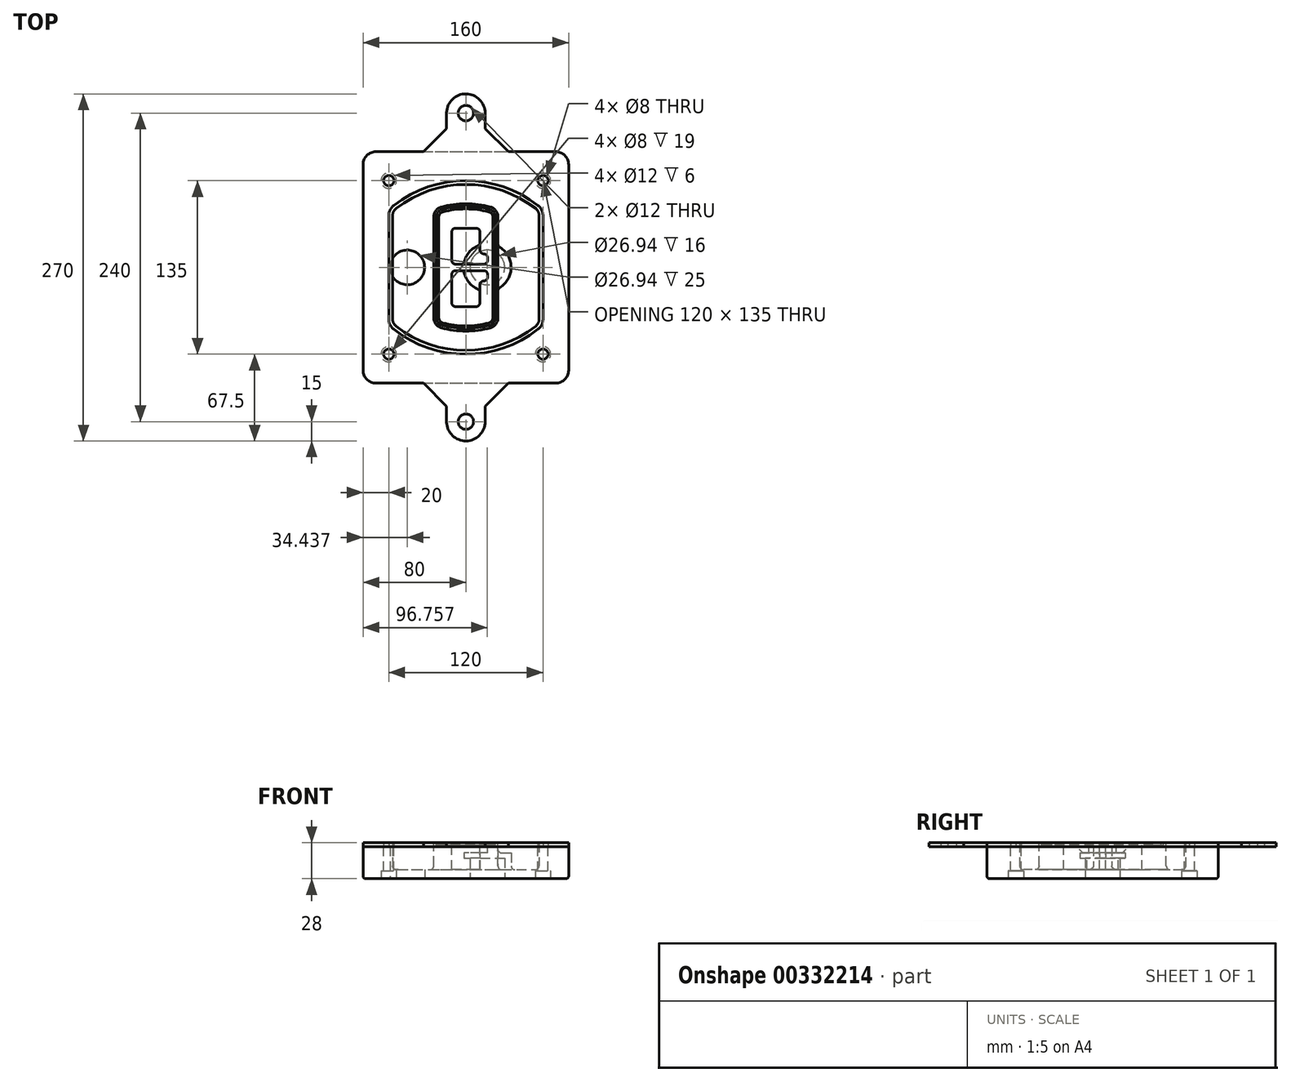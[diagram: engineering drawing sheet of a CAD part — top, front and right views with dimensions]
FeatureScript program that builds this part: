
annotation { "Feature Type Name" : "Feature", "Feature Type Description" : "" }
export const myFeature = defineFeature(function(context is Context, id is Id, definition is map)
    precondition{}
    {
        {
            var Q0;
            Q0=qCreatedBy(makeId("Top.planeOp"),FACE);
            var sketch = newSketch(context, id + "F0", { "sketchPlane" : qUnion([Q0])});
            skPoint(sketch, "E0.rect.middle", {"position": v(0, 0) * mm});
            skLineSegment(sketch, "E1.bottom", {"start": v(-70, -90) * mm, "end": v(70, -90) * mm});
            skLineSegment(sketch, "E1.top", {"start": v(-70, 90) * mm, "end": v(70, 90) * mm});
            skLineSegment(sketch, "E1.left", {"start": v(-80, -80) * mm, "end": v(-80, 80) * mm});
            skLineSegment(sketch, "E1.right", {"start": v(80, -80) * mm, "end": v(80, 80) * mm});
            skLineSegment(sketch, "E2", {"start": v(-80, 90) * mm, "end": v(80, -90) * mm, "construction": true});
            skLineSegment(sketch, "E3", {"start": v(80, 90) * mm, "end": v(-80, -90) * mm, "construction": true});
            skCircle(sketch, "E4", {"center": v(-60, 67.5) * mm, "radius": 4 * mm});
            skCircle(sketch, "E5", {"center": v(60, 67.5) * mm, "radius": 4 * mm});
            skCircle(sketch, "E6", {"center": v(60, -67.5) * mm, "radius": 4 * mm});
            skCircle(sketch, "E7", {"center": v(-60, -67.5) * mm, "radius": 4 * mm});
            skLineSegment(sketch, "E8", {"start": v(-60, 67.5) * mm, "end": v(60, 67.5) * mm, "construction": true});
            skLineSegment(sketch, "E9", {"start": v(60, 67.5) * mm, "end": v(60, -67.5) * mm, "construction": true});
            skLineSegment(sketch, "E10", {"start": v(60, -67.5) * mm, "end": v(-60, -67.5) * mm, "construction": true});
            skLineSegment(sketch, "E11", {"start": v(-60, -67.5) * mm, "end": v(-60, 67.5) * mm, "construction": true});
            skLineSegment(sketch, "E12", {"start": v(-60, 40.3) * mm, "end": v(-60, -40.3) * mm});
            skLineSegment(sketch, "E13", {"start": v(60, 40.3) * mm, "end": v(60, -40.3) * mm});
            skArc(sketch, "E14", {"start": v(56.15, 48.18) * mm, "mid": v(0, 67.5) * mm, "end": v(-56.15, 48.18) * mm});
            skArc(sketch, "E15", {"start": v(-56.15, -48.18) * mm, "mid": v(0, -67.5) * mm, "end": v(56.15, -48.18) * mm});
            skLineSegment(sketch, "E16", {"start": v(-60, 0) * mm, "end": v(60, 0) * mm, "construction": true});
            skPoint(sketch, "E17.visualSharp", {"position": v(-60, -45) * mm});
            skArc(sketch, "E17.filletArc", {"start": v(-60, -40.3) * mm, "mid": v(-58.99, -44.68) * mm, "end": v(-56.15, -48.18) * mm});
            skPoint(sketch, "E18.visualSharp", {"position": v(-60, 45) * mm});
            skArc(sketch, "E18.filletArc", {"start": v(-56.15, 48.18) * mm, "mid": v(-58.99, 44.68) * mm, "end": v(-60, 40.3) * mm});
            skPoint(sketch, "E19.visualSharp", {"position": v(60, 45) * mm});
            skArc(sketch, "E19.filletArc", {"start": v(60, 40.3) * mm, "mid": v(58.99, 44.68) * mm, "end": v(56.15, 48.18) * mm});
            skPoint(sketch, "E20.visualSharp", {"position": v(60, -45) * mm});
            skArc(sketch, "E20.filletArc", {"start": v(56.15, -48.18) * mm, "mid": v(58.99, -44.68) * mm, "end": v(60, -40.3) * mm});
            skPoint(sketch, "E21.visualSharp", {"position": v(-80, 90) * mm});
            skArc(sketch, "E21.filletArc", {"start": v(-70, 90) * mm, "mid": v(-77.07, 87.07) * mm, "end": v(-80, 80) * mm});
            skPoint(sketch, "E22.visualSharp", {"position": v(80, 90) * mm});
            skArc(sketch, "E22.filletArc", {"start": v(80, 80) * mm, "mid": v(77.07, 87.07) * mm, "end": v(70, 90) * mm});
            skPoint(sketch, "E23.visualSharp", {"position": v(80, -90) * mm});
            skArc(sketch, "E23.filletArc", {"start": v(70, -90) * mm, "mid": v(77.07, -87.07) * mm, "end": v(80, -80) * mm});
            skPoint(sketch, "E24.visualSharp", {"position": v(-80, -90) * mm});
            skArc(sketch, "E24.filletArc", {"start": v(-80, -80) * mm, "mid": v(-77.07, -87.07) * mm, "end": v(-70, -90) * mm});
            skArc(sketch, "E25.0", {"start": v(57, 40.3) * mm, "mid": v(56.3, 43.36) * mm, "end": v(54.3, 45.81) * mm});
            skLineSegment(sketch, "E25.1", {"start": v(57, 40.3) * mm, "end": v(57, -40.3) * mm});
            skArc(sketch, "E25.2", {"start": v(54.3, -45.81) * mm, "mid": v(56.3, -43.36) * mm, "end": v(57, -40.3) * mm});
            skArc(sketch, "E25.3", {"start": v(-54.3, -45.81) * mm, "mid": v(0, -64.5) * mm, "end": v(54.3, -45.81) * mm});
            skArc(sketch, "E25.4", {"start": v(-57, -40.3) * mm, "mid": v(-56.3, -43.36) * mm, "end": v(-54.3, -45.81) * mm});
            skArc(sketch, "E25.5", {"start": v(54.3, 45.81) * mm, "mid": v(0, 64.5) * mm, "end": v(-54.3, 45.81) * mm});
            skLineSegment(sketch, "E25.6", {"start": v(-57, 40.3) * mm, "end": v(-57, -40.3) * mm});
            skArc(sketch, "E25.7", {"start": v(-54.3, 45.81) * mm, "mid": v(-56.3, 43.36) * mm, "end": v(-57, 40.3) * mm});
            skArc(sketch, "E26.0", {"start": v(-58.62, 51.33) * mm, "mid": v(-62.58, 46.43) * mm, "end": v(-64, 40.3) * mm});
            skArc(sketch, "E26.1", {"start": v(58.62, 51.33) * mm, "mid": v(0, 71.5) * mm, "end": v(-58.62, 51.33) * mm});
            skArc(sketch, "E26.2", {"start": v(64, 40.3) * mm, "mid": v(62.58, 46.43) * mm, "end": v(58.62, 51.33) * mm});
            skLineSegment(sketch, "E26.3", {"start": v(64, 40.3) * mm, "end": v(64, -40.3) * mm});
            skArc(sketch, "E26.4", {"start": v(58.62, -51.33) * mm, "mid": v(62.58, -46.43) * mm, "end": v(64, -40.3) * mm});
            skLineSegment(sketch, "E26.5", {"start": v(-64, 40.3) * mm, "end": v(-64, -40.3) * mm});
            skArc(sketch, "E26.6", {"start": v(-58.62, -51.33) * mm, "mid": v(0, -71.5) * mm, "end": v(58.62, -51.33) * mm});
            skArc(sketch, "E26.7", {"start": v(-64, -40.3) * mm, "mid": v(-62.58, -46.43) * mm, "end": v(-58.62, -51.33) * mm});
            skSolve(sketch);
        }
        {
            var Q0;
            Q0=makeQuery(id+"F0.imprint","IMPRINT",FACE,{"disambiguationData":[TD([[makeQuery(id+"F0.imprint","IMPRINT",EDGE,{"derivedFrom":sQuery(id+"F0.wireOp",EDGE,"E1.bottom")}),1.0]])]});
            var Q1;
            Q1=makeQuery(id+"F0.imprint","IMPRINT",FACE,{"disambiguationData":[TD([[makeQuery(id+"F0.imprint","IMPRINT",EDGE,{"derivedFrom":sQuery(id+"F0.wireOp",EDGE,"E12")}),1.0]])]});
            var Q2;
            Q2=makeQuery(id+"F0.imprint","IMPRINT",FACE,{"disambiguationData":[TD([[makeQuery(id+"F0.imprint","IMPRINT",EDGE,{"derivedFrom":sQuery(id+"F0.wireOp",EDGE,"E25.0")}),1.0]])]});
            var Q3;
            Q3=makeQuery(id+"F0.imprint","IMPRINT",FACE,{"disambiguationData":[TD([[makeQuery(id+"F0.imprint","IMPRINT",EDGE,{"derivedFrom":sQuery(id+"F0.wireOp",EDGE,"E12")}),-1.0]])]});
            extrude(context, id + "F1", {"entities" : qUnion([Q0, Q1, Q2, Q3]), "oppositeDirection" : true, "depth" : 25 * mm});
        }
        {
            var Q0;
            Q0=makeQuery(id+"F0.imprint","IMPRINT",FACE,{"disambiguationData":[TD([[makeQuery(id+"F0.imprint","IMPRINT",EDGE,{"derivedFrom":sQuery(id+"F0.wireOp",EDGE,"E12")}),1.0]])]});
            extrude(context, id + "F2", {"entities" : qUnion([Q0]), "operationType" : NewBodyOperationType.ADD, "depth" : 3 * mm});
        }
        {
            var Q0;
            Q0=makeQuery(id+"F0.imprint","IMPRINT",FACE,{"disambiguationData":[TD([[makeQuery(id+"F0.imprint","IMPRINT",EDGE,{"derivedFrom":sQuery(id+"F0.wireOp",EDGE,"E25.0")}),1.0]])]});
            extrude(context, id + "F3", {"entities" : qUnion([Q0]), "operationType" : NewBodyOperationType.REMOVE, "oppositeDirection" : true, "depth" : 18 * mm});
        }
        {
            var Q0;
            Q0=makeQuery(id+"F2.opExtrude","CAP_FACE",FACE,{"disambiguationData":[OSD([sQuery(id+"F0.wireOp",EDGE,"E12"),sQuery(id+"F0.wireOp",EDGE,"E13"),sQuery(id+"F0.wireOp",EDGE,"E14"),sQuery(id+"F0.wireOp",EDGE,"E15"),sQuery(id+"F0.wireOp",EDGE,"E17.filletArc"),sQuery(id+"F0.wireOp",EDGE,"E18.filletArc"),sQuery(id+"F0.wireOp",EDGE,"E19.filletArc"),sQuery(id+"F0.wireOp",EDGE,"E20.filletArc"),sQuery(id+"F0.wireOp",EDGE,"E25.0"),sQuery(id+"F0.wireOp",EDGE,"E25.1"),sQuery(id+"F0.wireOp",EDGE,"E25.2"),sQuery(id+"F0.wireOp",EDGE,"E25.3"),sQuery(id+"F0.wireOp",EDGE,"E25.4"),sQuery(id+"F0.wireOp",EDGE,"E25.5"),sQuery(id+"F0.wireOp",EDGE,"E25.6"),sQuery(id+"F0.wireOp",EDGE,"E25.7")])],"isStart":false});
            var sketch = newSketch(context, id + "F4", { "sketchPlane" : qUnion([Q0])});
            skArc(sketch, "E27.0", {"start": v(-19.08, -46.97) * mm, "mid": v(0, -49.5) * mm, "end": v(19.08, -46.97) * mm});
            skArc(sketch, "E28.0", {"start": v(19.08, 46.97) * mm, "mid": v(0, 49.5) * mm, "end": v(-19.08, 46.97) * mm});
            skLineSegment(sketch, "E29", {"start": v(-25, 39.25) * mm, "end": v(-25, -39.25) * mm});
            skLineSegment(sketch, "E30", {"start": v(25, 39.25) * mm, "end": v(25, -39.25) * mm});
            skLineSegment(sketch, "E31", {"start": v(-25, 45.1) * mm, "end": v(25, 45.1) * mm, "construction": true});
            skLineSegment(sketch, "E32", {"start": v(-25, -45.1) * mm, "end": v(25, -45.1) * mm, "construction": true});
            skPoint(sketch, "E33.visualSharp", {"position": v(-25, 45.1) * mm});
            skArc(sketch, "E33.filletArc", {"start": v(-19.08, 46.97) * mm, "mid": v(-23.35, 44.11) * mm, "end": v(-25, 39.25) * mm});
            skPoint(sketch, "E34.visualSharp", {"position": v(25, 45.1) * mm});
            skArc(sketch, "E34.filletArc", {"start": v(25, 39.25) * mm, "mid": v(23.35, 44.11) * mm, "end": v(19.08, 46.97) * mm});
            skPoint(sketch, "E35.visualSharp", {"position": v(25, -45.1) * mm});
            skArc(sketch, "E35.filletArc", {"start": v(19.08, -46.97) * mm, "mid": v(23.35, -44.11) * mm, "end": v(25, -39.25) * mm});
            skPoint(sketch, "E36.visualSharp", {"position": v(-25, -45.1) * mm});
            skArc(sketch, "E36.filletArc", {"start": v(-25, -39.25) * mm, "mid": v(-23.35, -44.11) * mm, "end": v(-19.08, -46.97) * mm});
            skArc(sketch, "E37.0", {"start": v(54.3, 45.81) * mm, "mid": v(0, 64.5) * mm, "end": v(-54.3, 45.81) * mm});
            skArc(sketch, "E37.1", {"start": v(-54.3, 45.81) * mm, "mid": v(-56.3, 43.36) * mm, "end": v(-57, 40.3) * mm});
            skLineSegment(sketch, "E37.2", {"start": v(-57, 40.3) * mm, "end": v(-57, -40.3) * mm});
            skArc(sketch, "E37.3", {"start": v(-57, -40.3) * mm, "mid": v(-56.3, -43.36) * mm, "end": v(-54.3, -45.81) * mm});
            skArc(sketch, "E37.4", {"start": v(-54.3, -45.81) * mm, "mid": v(0, -64.5) * mm, "end": v(54.3, -45.81) * mm});
            skArc(sketch, "E37.5", {"start": v(54.3, -45.81) * mm, "mid": v(56.3, -43.36) * mm, "end": v(57, -40.3) * mm});
            skLineSegment(sketch, "E37.6", {"start": v(57, 40.3) * mm, "end": v(57, -40.3) * mm});
            skArc(sketch, "E37.7", {"start": v(57, 40.3) * mm, "mid": v(56.3, 43.36) * mm, "end": v(54.3, 45.81) * mm});
            skLineSegment(sketch, "E38.0", {"start": v(23, 39.25) * mm, "end": v(23, -39.25) * mm});
            skArc(sketch, "E38.1", {"start": v(18.56, -45.04) * mm, "mid": v(21.76, -42.9) * mm, "end": v(23, -39.25) * mm});
            skArc(sketch, "E38.2", {"start": v(-18.56, -45.04) * mm, "mid": v(0, -47.5) * mm, "end": v(18.56, -45.04) * mm});
            skArc(sketch, "E38.3", {"start": v(-23, -39.25) * mm, "mid": v(-21.76, -42.9) * mm, "end": v(-18.56, -45.04) * mm});
            skLineSegment(sketch, "E38.4", {"start": v(-23, 39.25) * mm, "end": v(-23, -39.25) * mm});
            skArc(sketch, "E38.5", {"start": v(23, 39.25) * mm, "mid": v(21.76, 42.9) * mm, "end": v(18.56, 45.04) * mm});
            skArc(sketch, "E38.6", {"start": v(-18.56, 45.04) * mm, "mid": v(-21.76, 42.9) * mm, "end": v(-23, 39.25) * mm});
            skArc(sketch, "E38.7", {"start": v(18.56, 45.04) * mm, "mid": v(0, 47.5) * mm, "end": v(-18.56, 45.04) * mm});
            skArc(sketch, "E39.0", {"start": v(21, 39.25) * mm, "mid": v(20.18, 41.68) * mm, "end": v(18.04, 43.1) * mm});
            skLineSegment(sketch, "E39.1", {"start": v(21, 39.25) * mm, "end": v(21, -39.25) * mm});
            skArc(sketch, "E39.2", {"start": v(18.04, -43.1) * mm, "mid": v(20.18, -41.68) * mm, "end": v(21, -39.25) * mm});
            skArc(sketch, "E39.3", {"start": v(-18.04, -43.1) * mm, "mid": v(0, -45.5) * mm, "end": v(18.04, -43.1) * mm});
            skArc(sketch, "E39.4", {"start": v(-21, -39.25) * mm, "mid": v(-20.18, -41.68) * mm, "end": v(-18.04, -43.1) * mm});
            skArc(sketch, "E39.5", {"start": v(18.04, 43.1) * mm, "mid": v(0, 45.5) * mm, "end": v(-18.04, 43.1) * mm});
            skLineSegment(sketch, "E39.6", {"start": v(-21, 39.25) * mm, "end": v(-21, -39.25) * mm});
            skArc(sketch, "E39.7", {"start": v(-18.04, 43.1) * mm, "mid": v(-20.18, 41.68) * mm, "end": v(-21, 39.25) * mm});
            skLineSegment(sketch, "E40", {"start": v(-25, 0) * mm, "end": v(25, 0) * mm, "construction": true});
            skLineSegment(sketch, "E41", {"start": v(-11, 5.5) * mm, "end": v(-11, 27.5) * mm});
            skLineSegment(sketch, "E42", {"start": v(-8, 30.5) * mm, "end": v(8, 30.5) * mm});
            skLineSegment(sketch, "E43", {"start": v(11, 27.5) * mm, "end": v(11, 13.5) * mm});
            skLineSegment(sketch, "E44", {"start": v(14, 10.5) * mm, "end": v(14, 10.5) * mm});
            skLineSegment(sketch, "E45", {"start": v(17, 7.5) * mm, "end": v(17, 5.5) * mm});
            skLineSegment(sketch, "E46", {"start": v(14, 2.5) * mm, "end": v(-8, 2.5) * mm});
            skPoint(sketch, "E47.visualSharp", {"position": v(-11, 30.5) * mm});
            skArc(sketch, "E47.filletArc", {"start": v(-8, 30.5) * mm, "mid": v(-10.12, 29.62) * mm, "end": v(-11, 27.5) * mm});
            skPoint(sketch, "E48.visualSharp", {"position": v(11, 30.5) * mm});
            skArc(sketch, "E48.filletArc", {"start": v(11, 27.5) * mm, "mid": v(10.12, 29.62) * mm, "end": v(8, 30.5) * mm});
            skPoint(sketch, "E49.visualSharp", {"position": v(11, 10.5) * mm});
            skArc(sketch, "E49.filletArc", {"start": v(11, 13.5) * mm, "mid": v(11.88, 11.38) * mm, "end": v(14, 10.5) * mm});
            skPoint(sketch, "E50.visualSharp", {"position": v(17, 10.5) * mm});
            skArc(sketch, "E50.filletArc", {"start": v(17, 7.5) * mm, "mid": v(16.12, 9.62) * mm, "end": v(14, 10.5) * mm});
            skPoint(sketch, "E51.visualSharp", {"position": v(17, 2.5) * mm});
            skArc(sketch, "E51.filletArc", {"start": v(14, 2.5) * mm, "mid": v(16.12, 3.38) * mm, "end": v(17, 5.5) * mm});
            skPoint(sketch, "E52.visualSharp", {"position": v(-11, 2.5) * mm});
            skArc(sketch, "E52.filletArc", {"start": v(-11, 5.5) * mm, "mid": v(-10.12, 3.38) * mm, "end": v(-8, 2.5) * mm});
            skLineSegment(sketch, "E53.0.MirrorCS", {"start": v(14, -2.5) * mm, "end": v(-8, -2.5) * mm});
            skArc(sketch, "E54.0.MirrorCS", {"start": v(-11, -5.5) * mm, "mid": v(-10.12, -3.38) * mm, "end": v(-8, -2.5) * mm});
            skLineSegment(sketch, "E55.0.MirrorCS", {"start": v(-11, -5.5) * mm, "end": v(-11, -27.5) * mm});
            skArc(sketch, "E56.0.MirrorCS", {"start": v(-8, -30.5) * mm, "mid": v(-10.12, -29.62) * mm, "end": v(-11, -27.5) * mm});
            skLineSegment(sketch, "E57.0.MirrorCS", {"start": v(-8, -30.5) * mm, "end": v(8, -30.5) * mm});
            skArc(sketch, "E58.0.MirrorCS", {"start": v(11, -27.5) * mm, "mid": v(10.12, -29.62) * mm, "end": v(8, -30.5) * mm});
            skLineSegment(sketch, "E59.0.MirrorCS", {"start": v(11, -27.5) * mm, "end": v(11, -13.5) * mm});
            skArc(sketch, "E60.0.MirrorCS", {"start": v(11, -13.5) * mm, "mid": v(11.88, -11.38) * mm, "end": v(14, -10.5) * mm});
            skArc(sketch, "E61.0.MirrorCS", {"start": v(17, -7.5) * mm, "mid": v(16.12, -9.62) * mm, "end": v(14, -10.5) * mm});
            skLineSegment(sketch, "E62.0.MirrorCS", {"start": v(17, -7.5) * mm, "end": v(17, -5.5) * mm});
            skArc(sketch, "E63.0.MirrorCS", {"start": v(14, -2.5) * mm, "mid": v(16.12, -3.38) * mm, "end": v(17, -5.5) * mm});
            skSolve(sketch);
        }
        {
            var Q0;
            Q0=makeQuery(id+"F4.imprint","IMPRINT",FACE,{"disambiguationData":[TD([[makeQuery(id+"F4.imprint","IMPRINT",EDGE,{"derivedFrom":sQuery(id+"F4.wireOp",EDGE,"E27.0")}),1.0]])]});
            var Q1;
            Q1=makeQuery(id+"F4.imprint","IMPRINT",FACE,{"disambiguationData":[TD([[makeQuery(id+"F4.imprint","IMPRINT",EDGE,{"derivedFrom":sQuery(id+"F4.wireOp",EDGE,"E38.0")}),-1.0]])]});
            var Q2;
            Q2=makeQuery(id+"F4.imprint","IMPRINT",FACE,{"disambiguationData":[TD([[makeQuery(id+"F4.imprint","IMPRINT",EDGE,{"derivedFrom":sQuery(id+"F4.wireOp",EDGE,"E39.0")}),1.0]])]});
            extrude(context, id + "F5", {"entities" : qUnion([Q0, Q1, Q2]), "operationType" : NewBodyOperationType.ADD, "endBound" : BoundingType.UP_TO_NEXT, "oppositeDirection" : true, "depth" : 25 * mm});
        }
        {
            var Q0;
            Q0=makeQuery(id+"F4.imprint","IMPRINT",FACE,{"disambiguationData":[TD([[makeQuery(id+"F4.imprint","IMPRINT",EDGE,{"derivedFrom":sQuery(id+"F4.wireOp",EDGE,"E38.0")}),-1.0]])]});
            extrude(context, id + "F6", {"entities" : qUnion([Q0]), "operationType" : NewBodyOperationType.REMOVE, "oppositeDirection" : true, "depth" : 2 * mm});
        }
        {
            var Q0;
            Q0=makeQuery(id+"F1.opExtrude","CAP_FACE",FACE,{"disambiguationData":[OSD([sQuery(id+"F0.wireOp",EDGE,"E1.bottom"),sQuery(id+"F0.wireOp",EDGE,"E1.top"),sQuery(id+"F0.wireOp",EDGE,"E1.left"),sQuery(id+"F0.wireOp",EDGE,"E1.right"),sQuery(id+"F0.wireOp",EDGE,"E4"),sQuery(id+"F0.wireOp",EDGE,"E5"),sQuery(id+"F0.wireOp",EDGE,"E6"),sQuery(id+"F0.wireOp",EDGE,"E7"),sQuery(id+"F0.wireOp",EDGE,"E21.filletArc"),sQuery(id+"F0.wireOp",EDGE,"E22.filletArc"),sQuery(id+"F0.wireOp",EDGE,"E23.filletArc"),sQuery(id+"F0.wireOp",EDGE,"E24.filletArc")])],"isStart":false});
            var sketch = newSketch(context, id + "F7", { "sketchPlane" : qUnion([Q0])});
            skCircle(sketch, "E64", {"center": v(16.76, 0) * mm, "radius": 13.47 * mm});
            skCircle(sketch, "E65", {"center": v(-45.56, 0) * mm, "radius": 13.47 * mm});
            skLineSegment(sketch, "E66", {"start": v(80, 0) * mm, "end": v(-80, 0) * mm});
            skCircle(sketch, "E67", {"center": v(16.76, 0) * mm, "radius": 18.47 * mm});
            skCircle(sketch, "E68", {"center": v(60, -67.5) * mm, "radius": 6 * mm});
            skCircle(sketch, "E69", {"center": v(-60, -67.5) * mm, "radius": 6 * mm});
            skCircle(sketch, "E70", {"center": v(-60, 67.5) * mm, "radius": 6 * mm});
            skCircle(sketch, "E71", {"center": v(60, 67.5) * mm, "radius": 6 * mm});
            skSolve(sketch);
        }
        {
            var Q0;
            {var subQ1=sQuery(id+"F7.wireOp",EDGE,"E66");var subQ4=sQuery(id+"F7.wireOp",EDGE,"E64");var subQ6=makeQuery(id+"F7.imprint","INTERSECT",VERTEX,{"disambiguationData":[OD(0.0)],"derivedFrom":[subQ4,subQ1]});Q0=makeQuery(id+"F7.imprint","IMPRINT",FACE,{"disambiguationData":[TD([[makeQuery(id+"F7.imprint","IMPRINT",EDGE,{"disambiguationData":[TD([[subQ6,-1.0]])],"derivedFrom":subQ4}),-1.0]])]});}
            var Q1;
            {var subQ0=sQuery(id+"F7.wireOp",EDGE,"E66");var subQ1=sQuery(id+"F7.wireOp",EDGE,"E64");var subQ3=makeQuery(id+"F7.imprint","INTERSECT",VERTEX,{"disambiguationData":[OD(0.0)],"derivedFrom":[subQ1,subQ0]});Q1=makeQuery(id+"F7.imprint","IMPRINT",FACE,{"disambiguationData":[TD([[makeQuery(id+"F7.imprint","IMPRINT",EDGE,{"disambiguationData":[TD([[subQ3,-1.0]])],"derivedFrom":subQ1}),1.0]])]});}
            var Q2;
            {var subQ0=sQuery(id+"F7.wireOp",EDGE,"E66");var subQ1=sQuery(id+"F7.wireOp",EDGE,"E64");var subQ3=makeQuery(id+"F7.imprint","INTERSECT",VERTEX,{"disambiguationData":[OD(0.0)],"derivedFrom":[subQ1,subQ0]});Q2=makeQuery(id+"F7.imprint","IMPRINT",FACE,{"disambiguationData":[TD([[makeQuery(id+"F7.imprint","IMPRINT",EDGE,{"disambiguationData":[TD([[subQ3,1.0]])],"derivedFrom":subQ1}),1.0]])]});}
            var Q3;
            {var subQ1=sQuery(id+"F7.wireOp",EDGE,"E66");var subQ4=sQuery(id+"F7.wireOp",EDGE,"E64");var subQ6=makeQuery(id+"F7.imprint","INTERSECT",VERTEX,{"disambiguationData":[OD(0.0)],"derivedFrom":[subQ4,subQ1]});Q3=makeQuery(id+"F7.imprint","IMPRINT",FACE,{"disambiguationData":[TD([[makeQuery(id+"F7.imprint","IMPRINT",EDGE,{"disambiguationData":[TD([[subQ6,1.0]])],"derivedFrom":subQ4}),-1.0]])]});}
            extrude(context, id + "F8", {"entities" : qUnion([Q0, Q1, Q2, Q3]), "operationType" : NewBodyOperationType.ADD, "oppositeDirection" : true, "depth" : 20 * mm});
        }
        {
            var Q0;
            {var subQ0=sQuery(id+"F7.wireOp",EDGE,"E66");var subQ1=sQuery(id+"F7.wireOp",EDGE,"E64");var subQ3=makeQuery(id+"F7.imprint","INTERSECT",VERTEX,{"disambiguationData":[OD(0.0)],"derivedFrom":[subQ1,subQ0]});Q0=makeQuery(id+"F7.imprint","IMPRINT",FACE,{"disambiguationData":[TD([[makeQuery(id+"F7.imprint","IMPRINT",EDGE,{"disambiguationData":[TD([[subQ3,-1.0]])],"derivedFrom":subQ1}),1.0]])]});}
            var Q1;
            {var subQ0=sQuery(id+"F7.wireOp",EDGE,"E66");var subQ1=sQuery(id+"F7.wireOp",EDGE,"E64");var subQ3=makeQuery(id+"F7.imprint","INTERSECT",VERTEX,{"disambiguationData":[OD(0.0)],"derivedFrom":[subQ1,subQ0]});Q1=makeQuery(id+"F7.imprint","IMPRINT",FACE,{"disambiguationData":[TD([[makeQuery(id+"F7.imprint","IMPRINT",EDGE,{"disambiguationData":[TD([[subQ3,1.0]])],"derivedFrom":subQ1}),1.0]])]});}
            extrude(context, id + "F9", {"entities" : qUnion([Q0, Q1]), "operationType" : NewBodyOperationType.REMOVE, "oppositeDirection" : true, "depth" : 16 * mm});
        }
        {
            var Q0;
            {var subQ0=sQuery(id+"F7.wireOp",EDGE,"E66");var subQ1=sQuery(id+"F7.wireOp",EDGE,"E65");var subQ3=makeQuery(id+"F7.imprint","INTERSECT",VERTEX,{"disambiguationData":[OD(0.0)],"derivedFrom":[subQ1,subQ0]});Q0=makeQuery(id+"F7.imprint","IMPRINT",FACE,{"disambiguationData":[TD([[makeQuery(id+"F7.imprint","IMPRINT",EDGE,{"disambiguationData":[TD([[subQ3,-1.0]])],"derivedFrom":subQ1}),1.0]])]});}
            var Q1;
            {var subQ0=sQuery(id+"F7.wireOp",EDGE,"E66");var subQ1=sQuery(id+"F7.wireOp",EDGE,"E65");var subQ3=makeQuery(id+"F7.imprint","INTERSECT",VERTEX,{"disambiguationData":[OD(0.0)],"derivedFrom":[subQ1,subQ0]});Q1=makeQuery(id+"F7.imprint","IMPRINT",FACE,{"disambiguationData":[TD([[makeQuery(id+"F7.imprint","IMPRINT",EDGE,{"disambiguationData":[TD([[subQ3,1.0]])],"derivedFrom":subQ1}),1.0]])]});}
            extrude(context, id + "F10", {"entities" : qUnion([Q0, Q1]), "operationType" : NewBodyOperationType.REMOVE, "oppositeDirection" : true, "depth" : 25 * mm});
        }
        {
            var Q0;
            Q0=makeQuery(id+"F7.imprint","IMPRINT",FACE,{"disambiguationData":[TD([[makeQuery(id+"F7.imprint","IMPRINT",EDGE,{"derivedFrom":sQuery(id+"F7.wireOp",EDGE,"E68")}),1.0]])]});
            var Q1;
            Q1=makeQuery(id+"F7.imprint","IMPRINT",FACE,{"disambiguationData":[TD([[makeQuery(id+"F7.imprint","IMPRINT",EDGE,{"derivedFrom":makeQuery(id+"F1.opExtrude","CAP_EDGE",EDGE,{"disambiguationData":[OSD([sQuery(id+"F0.wireOp",EDGE,"E5")])],"isStart":false})}),-1.0]])]});
            var Q2;
            Q2=makeQuery(id+"F7.imprint","IMPRINT",FACE,{"disambiguationData":[TD([[makeQuery(id+"F7.imprint","IMPRINT",EDGE,{"derivedFrom":sQuery(id+"F7.wireOp",EDGE,"E69")}),1.0]])]});
            var Q3;
            Q3=makeQuery(id+"F7.imprint","IMPRINT",FACE,{"disambiguationData":[TD([[makeQuery(id+"F7.imprint","IMPRINT",EDGE,{"derivedFrom":makeQuery(id+"F1.opExtrude","CAP_EDGE",EDGE,{"disambiguationData":[OSD([sQuery(id+"F0.wireOp",EDGE,"E4")])],"isStart":false})}),-1.0]])]});
            var Q4;
            Q4=makeQuery(id+"F7.imprint","IMPRINT",FACE,{"disambiguationData":[TD([[makeQuery(id+"F7.imprint","IMPRINT",EDGE,{"derivedFrom":sQuery(id+"F7.wireOp",EDGE,"E70")}),1.0]])]});
            var Q5;
            Q5=makeQuery(id+"F7.imprint","IMPRINT",FACE,{"disambiguationData":[TD([[makeQuery(id+"F7.imprint","IMPRINT",EDGE,{"derivedFrom":makeQuery(id+"F1.opExtrude","CAP_EDGE",EDGE,{"disambiguationData":[OSD([sQuery(id+"F0.wireOp",EDGE,"E7")])],"isStart":false})}),-1.0]])]});
            var Q6;
            Q6=makeQuery(id+"F7.imprint","IMPRINT",FACE,{"disambiguationData":[TD([[makeQuery(id+"F7.imprint","IMPRINT",EDGE,{"derivedFrom":sQuery(id+"F7.wireOp",EDGE,"E71")}),1.0]])]});
            var Q7;
            Q7=makeQuery(id+"F7.imprint","IMPRINT",FACE,{"disambiguationData":[TD([[makeQuery(id+"F7.imprint","IMPRINT",EDGE,{"derivedFrom":makeQuery(id+"F1.opExtrude","CAP_EDGE",EDGE,{"disambiguationData":[OSD([sQuery(id+"F0.wireOp",EDGE,"E6")])],"isStart":false})}),-1.0]])]});
            extrude(context, id + "F11", {"entities" : qUnion([Q0, Q1, Q2, Q3, Q4, Q5, Q6, Q7]), "operationType" : NewBodyOperationType.REMOVE, "oppositeDirection" : true, "depth" : 6 * mm});
        }
        {
            var Q0;
            Q0=makeQuery(id+"F9.boolean.opBoolean","COPY",FACE,{"derivedFrom":makeQuery(id+"F9.opExtrude","CAP_FACE",FACE,{"disambiguationData":[OSD([sQuery(id+"F7.wireOp",EDGE,"E64")])],"isStart":false})});
            var sketch = newSketch(context, id + "F12", { "sketchPlane" : qUnion([Q0])});
            skArc(sketch, "E72.0", {"start": v(11, 17.55) * mm, "mid": v(2.57, 11.82) * mm, "end": v(-1.54, 2.5) * mm});
            skArc(sketch, "E72.1", {"start": v(-1.54, -2.5) * mm, "mid": v(2.57, -11.82) * mm, "end": v(11, -17.55) * mm});
            skLineSegment(sketch, "E73", {"start": v(-1.54, -2.5) * mm, "end": v(14, -2.5) * mm});
            skLineSegment(sketch, "E74.0", {"start": v(14, 2.5) * mm, "end": v(-1.54, 2.5) * mm});
            skArc(sketch, "E74.1", {"start": v(14, 2.5) * mm, "mid": v(16.12, 3.38) * mm, "end": v(17, 5.5) * mm});
            skLineSegment(sketch, "E74.2", {"start": v(17, 7.5) * mm, "end": v(17, 5.5) * mm});
            skArc(sketch, "E74.3", {"start": v(17, 7.5) * mm, "mid": v(16.12, 9.62) * mm, "end": v(14, 10.5) * mm});
            skArc(sketch, "E74.4", {"start": v(11, 13.5) * mm, "mid": v(11.88, 11.38) * mm, "end": v(14, 10.5) * mm});
            skLineSegment(sketch, "E74.5", {"start": v(11, 17.55) * mm, "end": v(11, 13.5) * mm});
            skLineSegment(sketch, "E74.7", {"start": v(14, -2.5) * mm, "end": v(-1.54, -2.5) * mm});
            skArc(sketch, "E74.8", {"start": v(14, -2.5) * mm, "mid": v(16.12, -3.38) * mm, "end": v(17, -5.5) * mm});
            skLineSegment(sketch, "E74.9", {"start": v(17, -7.5) * mm, "end": v(17, -5.5) * mm});
            skArc(sketch, "E74.10", {"start": v(17, -7.5) * mm, "mid": v(16.12, -9.62) * mm, "end": v(14, -10.5) * mm});
            skArc(sketch, "E74.11", {"start": v(11, -13.5) * mm, "mid": v(11.88, -11.38) * mm, "end": v(14, -10.5) * mm});
            skLineSegment(sketch, "E74.12", {"start": v(11, -17.55) * mm, "end": v(11, -13.5) * mm});
            skPoint(sketch, "E75.orphan", {"position": v(11, -27.5) * mm});
            skPoint(sketch, "E76.orphan", {"position": v(-8, -2.5) * mm});
            skPoint(sketch, "E77.orphan", {"position": v(-8, 2.5) * mm});
            skPoint(sketch, "E78.orphan", {"position": v(11, 27.5) * mm});
            skSolve(sketch);
        }
        {
            var Q0;
            {var subQ7=sQuery(id+"F12.wireOp",EDGE,"E72.0");var subQ14=sQuery(id+"F12.wireOp",EDGE,"E72.1");var subQ16=sQuery(id+"F12.wireOp",EDGE,"E74.1");var subQ18=sQuery(id+"F12.wireOp",EDGE,"E74.8");Q0=qUnion([makeQuery(id+"F12.imprint","IMPRINT",FACE,{"disambiguationData":[TD([[makeQuery(id+"F12.imprint","IMPRINT",EDGE,{"derivedFrom":subQ7}),1.0]])]}),makeQuery(id+"F12.imprint","IMPRINT",FACE,{"disambiguationData":[TD([[makeQuery(id+"F12.imprint","IMPRINT",EDGE,{"derivedFrom":subQ14}),1.0]])]}),makeQuery(id+"F12.imprint","IMPRINT",FACE,{"disambiguationData":[TD([[makeQuery(id+"F12.imprint","IMPRINT",EDGE,{"derivedFrom":subQ16}),1.0]])]}),makeQuery(id+"F12.imprint","IMPRINT",FACE,{"disambiguationData":[TD([[makeQuery(id+"F12.imprint","IMPRINT",EDGE,{"derivedFrom":subQ18}),-1.0]])]})]);}
            var Q1;
            Q1=makeQuery(id+"F5.boolean.opBoolean","SPLIT",FACE,{"disambiguationData":[TD([makeQuery(id+"F5.opExtrude","SWEPT_FACE",FACE,{"disambiguationData":[OSD([sQuery(id+"F4.wireOp",EDGE,"E41")])]})])],"derivedFrom":makeQuery(id+"F3.boolean.opBoolean","COPY",FACE,{"derivedFrom":makeQuery(id+"F3.opExtrude","CAP_FACE",FACE,{"disambiguationData":[OSD([sQuery(id+"F0.wireOp",EDGE,"E25.0"),sQuery(id+"F0.wireOp",EDGE,"E25.1"),sQuery(id+"F0.wireOp",EDGE,"E25.2"),sQuery(id+"F0.wireOp",EDGE,"E25.3"),sQuery(id+"F0.wireOp",EDGE,"E25.4"),sQuery(id+"F0.wireOp",EDGE,"E25.5"),sQuery(id+"F0.wireOp",EDGE,"E25.6"),sQuery(id+"F0.wireOp",EDGE,"E25.7")])],"isStart":false})})});
            extrude(context, id + "F13", {"entities" : qUnion([Q0]), "operationType" : NewBodyOperationType.REMOVE, "endBound" : BoundingType.UP_TO_SURFACE, "endBoundEntityFace" : qUnion([Q1]), "depth" : 25 * mm});
        }
        {
            var Q0;
            Q0=makeQuery(id+"F3.boolean.opBoolean","COPY",EDGE,{"derivedFrom":makeQuery(id+"F3.opExtrude","CAP_EDGE",EDGE,{"disambiguationData":[OSD([sQuery(id+"F0.wireOp",EDGE,"E25.6")])],"isStart":false})});
            var Q1;
            Q1=makeQuery(id+"F8.boolean.opBoolean","INTERSECT",EDGE,{"derivedFrom":[makeQuery(id+"F5.opExtrude","SWEPT_FACE",FACE,{"disambiguationData":[OSD([sQuery(id+"F4.wireOp",EDGE,"E30")])]}),makeQuery(id+"F8.opExtrude","CAP_FACE",FACE,{"disambiguationData":[OSD([sQuery(id+"F7.wireOp",EDGE,"E67")])],"isStart":false})]});
            var Q2;
            Q2=makeQuery(id+"F8.boolean.opBoolean","INTERSECT",EDGE,{"disambiguationData":[OD(1.0)],"derivedFrom":[makeQuery(id+"F5.opExtrude","SWEPT_FACE",FACE,{"disambiguationData":[OSD([sQuery(id+"F4.wireOp",EDGE,"E30")])]}),makeQuery(id+"F8.opExtrude","SWEPT_FACE",FACE,{"disambiguationData":[OSD([sQuery(id+"F7.wireOp",EDGE,"E67")])]})]});
            var Q3;
            {var subQ0=sQuery(id+"F4.wireOp",EDGE,"E30");Q3=makeQuery(id+"F8.boolean.opBoolean","SPLIT",EDGE,{"disambiguationData":[TD([makeQuery(id+"F5.opExtrude","SWEPT_FACE",FACE,{"disambiguationData":[OSD([sQuery(id+"F4.wireOp",EDGE,"E35.filletArc")])]})])],"derivedFrom":makeQuery(id+"F5.opExtrude","CAP_EDGE",EDGE,{"disambiguationData":[OSD([subQ0])],"isStart":false})});}
            var Q4;
            {var subQ0=sQuery(id+"F0.wireOp",EDGE,"E25.7");var subQ1=sQuery(id+"F0.wireOp",EDGE,"E25.1");var subQ2=sQuery(id+"F0.wireOp",EDGE,"E25.6");var subQ3=sQuery(id+"F0.wireOp",EDGE,"E25.5");var subQ4=sQuery(id+"F0.wireOp",EDGE,"E25.4");var subQ5=sQuery(id+"F0.wireOp",EDGE,"E25.0");var subQ6=sQuery(id+"F0.wireOp",EDGE,"E25.2");var subQ7=sQuery(id+"F0.wireOp",EDGE,"E25.3");Q4=makeQuery(id+"F8.boolean.opBoolean","INTERSECT",EDGE,{"derivedFrom":[makeQuery(id+"F5.boolean.opBoolean","SPLIT",FACE,{"disambiguationData":[TD([makeQuery(id+"F2.opExtrude","SWEPT_FACE",FACE,{"disambiguationData":[OSD([subQ5])]})])],"derivedFrom":makeQuery(id+"F3.boolean.opBoolean","COPY",FACE,{"derivedFrom":makeQuery(id+"F3.opExtrude","CAP_FACE",FACE,{"disambiguationData":[OSD([subQ5,subQ1,subQ6,subQ7,subQ4,subQ3,subQ2,subQ0])],"isStart":false})})}),makeQuery(id+"F8.opExtrude","SWEPT_FACE",FACE,{"disambiguationData":[OSD([sQuery(id+"F7.wireOp",EDGE,"E67")])]})]});}
            var Q5;
            Q5=makeQuery(id+"F8.boolean.opBoolean","INTERSECT",EDGE,{"disambiguationData":[OD(0.0)],"derivedFrom":[makeQuery(id+"F5.opExtrude","SWEPT_FACE",FACE,{"disambiguationData":[OSD([sQuery(id+"F4.wireOp",EDGE,"E30")])]}),makeQuery(id+"F8.opExtrude","SWEPT_FACE",FACE,{"disambiguationData":[OSD([sQuery(id+"F7.wireOp",EDGE,"E67")])]})]});
            fillet(context, id + "F14", {"entities" : qUnion([Q0, Q1, Q2, Q3, Q4, Q5]), "radius" : 3 * mm, "tangentPropagation" : true, "allowEdgeOverflow" : false});
        }
        {
            var Q0;
            Q0=makeQuery(id+"F1.opExtrude","CAP_EDGE",EDGE,{"disambiguationData":[OSD([sQuery(id+"F0.wireOp",EDGE,"E1.bottom")])],"isStart":false});
            fillet(context, id + "F15", {"entities" : qUnion([Q0]), "radius" : 2 * mm, "tangentPropagation" : true, "allowEdgeOverflow" : false});
        }
        {
            var Q0;
            {var subQ0=sQuery(id+"F0.wireOp",EDGE,"E21.filletArc");var subQ1=sQuery(id+"F0.wireOp",EDGE,"E7");var subQ2=sQuery(id+"F0.wireOp",EDGE,"E6");var subQ3=sQuery(id+"F0.wireOp",EDGE,"E5");var subQ4=sQuery(id+"F0.wireOp",EDGE,"E4");var subQ5=sQuery(id+"F0.wireOp",EDGE,"E22.filletArc");var subQ6=sQuery(id+"F0.wireOp",EDGE,"E1.bottom");var subQ7=sQuery(id+"F0.wireOp",EDGE,"E1.right");var subQ8=sQuery(id+"F0.wireOp",EDGE,"E1.top");var subQ9=sQuery(id+"F0.wireOp",EDGE,"E1.left");var subQ10=sQuery(id+"F0.wireOp",EDGE,"E23.filletArc");var subQ11=sQuery(id+"F0.wireOp",EDGE,"E24.filletArc");Q0=makeQuery(id+"F2.boolean.opBoolean","SPLIT",FACE,{"disambiguationData":[TD([makeQuery(id+"F1.opExtrude","SWEPT_FACE",FACE,{"disambiguationData":[OSD([subQ6])]})])],"derivedFrom":makeQuery(id+"F1.opExtrude","CAP_FACE",FACE,{"disambiguationData":[OSD([subQ6,subQ8,subQ9,subQ7,subQ4,subQ3,subQ2,subQ1,subQ0,subQ5,subQ10,subQ11])],"isStart":true})});}
            var sketch = newSketch(context, id + "F16", { "sketchPlane" : qUnion([Q0])});
            skLineSegment(sketch, "E79", {"start": v(33, 90) * mm, "end": v(15, 108) * mm});
            skLineSegment(sketch, "E80", {"start": v(-15, 108) * mm, "end": v(-15, 120.38) * mm});
            skLineSegment(sketch, "E81", {"start": v(15, 108) * mm, "end": v(15, 120) * mm});
            skArc(sketch, "E82", {"start": v(15, 120) * mm, "mid": v(0.19, 135) * mm, "end": v(-15, 120.38) * mm});
            skPoint(sketch, "E83.start.orphan", {"position": v(0, 90) * mm});
            skLineSegment(sketch, "E84", {"start": v(0, 90) * mm, "end": v(0, 120) * mm});
            skCircle(sketch, "E85", {"center": v(0, 120) * mm, "radius": 6 * mm});
            skLineSegment(sketch, "E86", {"start": v(-15, 108) * mm, "end": v(-33, 90) * mm});
            skLineSegment(sketch, "E87", {"start": v(-80, 0) * mm, "end": v(80, 0) * mm, "construction": true});
            skLineSegment(sketch, "E88.MirrorCS", {"start": v(-15, -108) * mm, "end": v(-33, -90) * mm});
            skLineSegment(sketch, "E89.MirrorCS", {"start": v(33, -90) * mm, "end": v(15, -108) * mm});
            skLineSegment(sketch, "E90.MirrorCS", {"start": v(-15, -108) * mm, "end": v(-15, -120.38) * mm});
            skLineSegment(sketch, "E91.MirrorCS", {"start": v(0, -90) * mm, "end": v(0, -120) * mm});
            skLineSegment(sketch, "E92.MirrorCS", {"start": v(15, -108) * mm, "end": v(15, -120) * mm});
            skArc(sketch, "E93.MirrorCS", {"start": v(15, -120) * mm, "mid": v(0.19, -135) * mm, "end": v(-15, -120.38) * mm});
            skCircle(sketch, "E94.MirrorC", {"center": v(0, -120) * mm, "radius": 6 * mm});
            skSolve(sketch);
        }
        {
            var Q0;
            Q0=makeQuery(id+"F16.imprint","IMPRINT",FACE,{"disambiguationData":[TD([[makeQuery(id+"F16.imprint","IMPRINT",EDGE,{"derivedFrom":makeQuery(id+"F1.opExtrude","CAP_EDGE",EDGE,{"disambiguationData":[OSD([sQuery(id+"F0.wireOp",EDGE,"E1.left")])],"isStart":true})}),-1.0]])]});
            var Q1;
            {var subQ0=sQuery(id+"F16.wireOp",EDGE,"E88.MirrorCS");Q1=makeQuery(id+"F16.imprint","IMPRINT",FACE,{"disambiguationData":[TD([[makeQuery(id+"F16.imprint","IMPRINT",EDGE,{"derivedFrom":subQ0}),-1.0]])]});}
            var Q2;
            {var subQ0=sQuery(id+"F16.wireOp",EDGE,"E79");Q2=makeQuery(id+"F16.imprint","IMPRINT",FACE,{"disambiguationData":[TD([[makeQuery(id+"F16.imprint","IMPRINT",EDGE,{"derivedFrom":subQ0}),1.0]])]});}
            var Q3;
            Q3=makeQuery(id+"F2.opExtrude","CAP_FACE",FACE,{"disambiguationData":[OSD([sQuery(id+"F0.wireOp",EDGE,"E12"),sQuery(id+"F0.wireOp",EDGE,"E13"),sQuery(id+"F0.wireOp",EDGE,"E14"),sQuery(id+"F0.wireOp",EDGE,"E15"),sQuery(id+"F0.wireOp",EDGE,"E17.filletArc"),sQuery(id+"F0.wireOp",EDGE,"E18.filletArc"),sQuery(id+"F0.wireOp",EDGE,"E19.filletArc"),sQuery(id+"F0.wireOp",EDGE,"E20.filletArc"),sQuery(id+"F0.wireOp",EDGE,"E25.0"),sQuery(id+"F0.wireOp",EDGE,"E25.1"),sQuery(id+"F0.wireOp",EDGE,"E25.2"),sQuery(id+"F0.wireOp",EDGE,"E25.3"),sQuery(id+"F0.wireOp",EDGE,"E25.4"),sQuery(id+"F0.wireOp",EDGE,"E25.5"),sQuery(id+"F0.wireOp",EDGE,"E25.6"),sQuery(id+"F0.wireOp",EDGE,"E25.7")])],"isStart":false});
            extrude(context, id + "F17", {"entities" : qUnion([Q0, Q1, Q2]), "endBound" : BoundingType.UP_TO_SURFACE, "endBoundEntityFace" : qUnion([Q3]), "depth" : 25 * mm});
        }
    });
